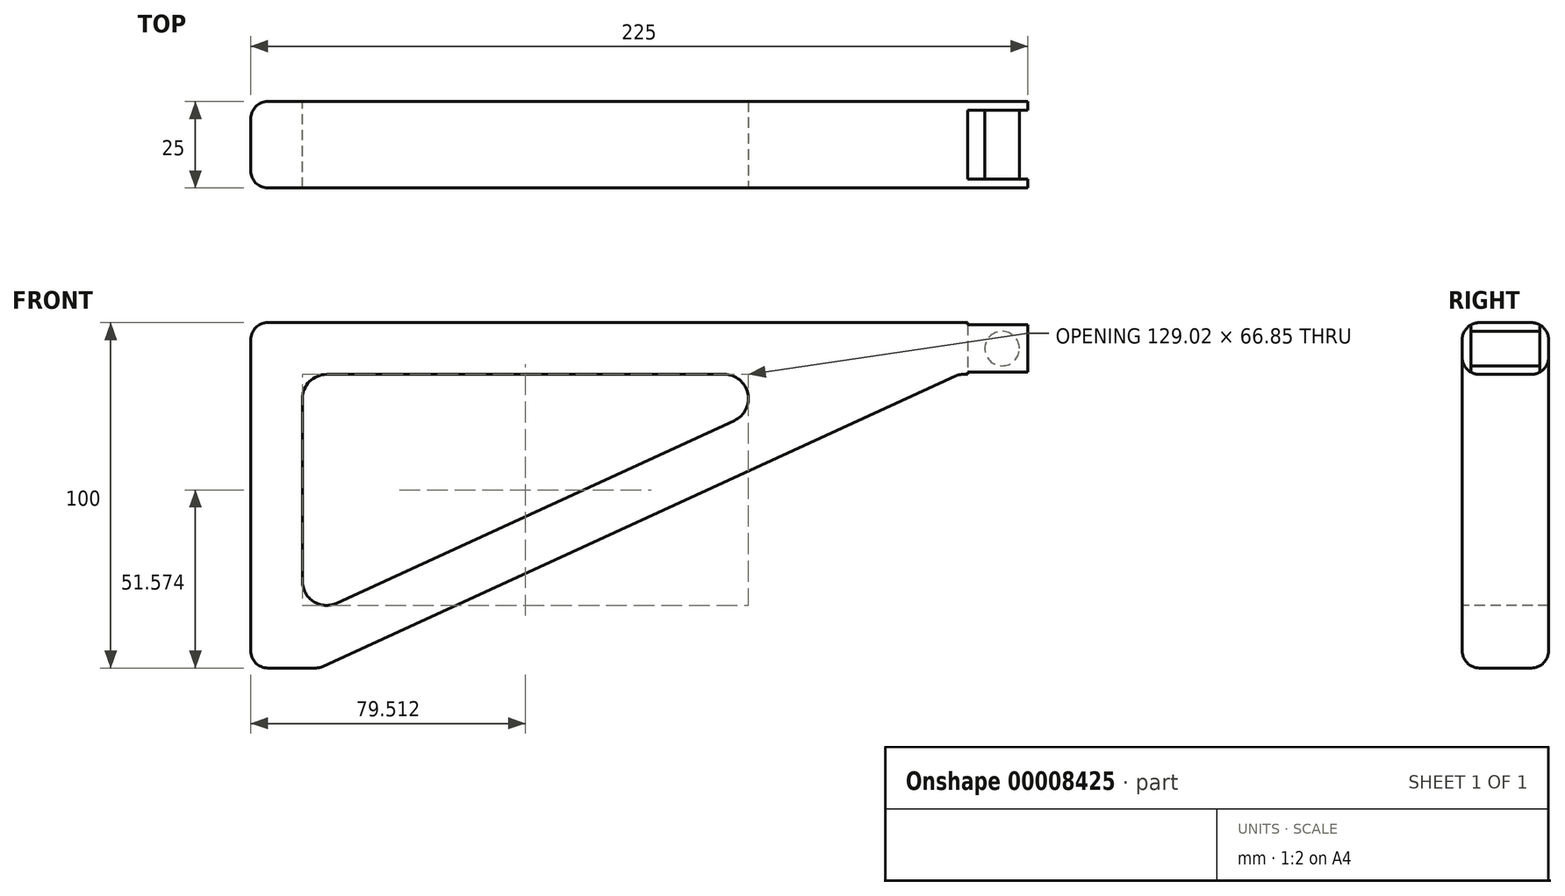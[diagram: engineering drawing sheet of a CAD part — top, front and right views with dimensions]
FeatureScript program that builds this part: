
annotation { "Feature Type Name" : "Feature", "Feature Type Description" : "" }
export const myFeature = defineFeature(function(context is Context, id is Id, definition is map)
    precondition{}
    {
        {
            var Q0;
            Q0=qCreatedBy(makeId("Front.planeOp"),FACE);
            var sketch = newSketch(context, id + "F0", { "sketchPlane" : qUnion([Q0])});
            skLineSegment(sketch, "E0", {"start": v(51.64, 0) * mm, "end": v(-173.36, 0) * mm});
            skLineSegment(sketch, "E1", {"start": v(-173.36, 0) * mm, "end": v(-173.36, -100) * mm});
            skLineSegment(sketch, "E2", {"start": v(-173.36, -100) * mm, "end": v(-153.36, -100) * mm});
            skLineSegment(sketch, "E3", {"start": v(-153.36, -100) * mm, "end": v(31.64, -15) * mm});
            skLineSegment(sketch, "E4", {"start": v(31.64, -15) * mm, "end": v(51.64, -15) * mm});
            skLineSegment(sketch, "E5", {"start": v(51.64, -15) * mm, "end": v(51.64, 0) * mm});
            skSolve(sketch);
        }
        {
            var Q0;
            Q0 = qSketchRegion(id + "F0", true);
            extrude(context, id + "F1", {"entities" : qUnion([Q0]), "depth" : 25 * mm});
        }
        {
            var Q0;
            Q0=makeQuery(id+"F1.opExtrude","SWEPT_FACE",FACE,{"disambiguationData":[OSD([sQuery(id+"F0.wireOp",EDGE,"E4")])]});
            var sketch = newSketch(context, id + "F2", { "sketchPlane" : qUnion([Q0])});
            skLineSegment(sketch, "E6.bottom", {"start": v(51.64, 2.5) * mm, "end": v(34.14, 2.5) * mm});
            skLineSegment(sketch, "E6.top", {"start": v(51.64, 22.5) * mm, "end": v(34.14, 22.5) * mm});
            skLineSegment(sketch, "E6.left", {"start": v(51.64, 2.5) * mm, "end": v(51.64, 22.5) * mm});
            skLineSegment(sketch, "E6.right", {"start": v(34.14, 2.5) * mm, "end": v(34.14, 22.5) * mm});
            skSolve(sketch);
        }
        {
            var Q0;
            Q0 = qSketchRegion(id + "F2", true);
            extrude(context, id + "F3", {"entities" : qUnion([Q0]), "operationType" : NewBodyOperationType.REMOVE, "oppositeDirection" : true, "depth" : 25 * mm});
        }
        {
            var Q0;
            Q0=makeQuery(id+"F1.opExtrude","CAP_FACE",FACE,{"disambiguationData":[OSD([sQuery(id+"F0.wireOp",EDGE,"E0"),sQuery(id+"F0.wireOp",EDGE,"E1"),sQuery(id+"F0.wireOp",EDGE,"E2"),sQuery(id+"F0.wireOp",EDGE,"E3"),sQuery(id+"F0.wireOp",EDGE,"E4"),sQuery(id+"F0.wireOp",EDGE,"E5")])],"isStart":false});
            var sketch = newSketch(context, id + "F4", { "sketchPlane" : qUnion([Q0])});
            skCircle(sketch, "E7", {"center": v(44.14, -7.5) * mm, "radius": 5 * mm});
            skSolve(sketch);
        }
        {
            var Q0;
            Q0 = qSketchRegion(id + "F4", true);
            extrude(context, id + "F5", {"entities" : qUnion([Q0]), "operationType" : NewBodyOperationType.ADD, "oppositeDirection" : true, "depth" : 25 * mm});
        }
        {
            var Q0;
            Q0=makeQuery(id+"F1.opExtrude","CAP_EDGE",EDGE,{"disambiguationData":[OSD([sQuery(id+"F0.wireOp",EDGE,"E1")])],"isStart":false});
            var Q1;
            Q1=makeQuery(id+"F1.opExtrude","CAP_EDGE",EDGE,{"disambiguationData":[OSD([sQuery(id+"F0.wireOp",EDGE,"E1")])],"isStart":true});
            var Q2;
            Q2=makeQuery(id+"F1.opExtrude","CAP_EDGE",EDGE,{"disambiguationData":[OSD([sQuery(id+"F0.wireOp",EDGE,"E0")])],"isStart":false});
            var Q3;
            Q3=makeQuery(id+"F1.opExtrude","CAP_EDGE",EDGE,{"disambiguationData":[OSD([sQuery(id+"F0.wireOp",EDGE,"E0")])],"isStart":true});
            var Q4;
            Q4=makeQuery(id+"F1.opExtrude","CAP_EDGE",EDGE,{"disambiguationData":[OSD([sQuery(id+"F0.wireOp",EDGE,"E4")])],"isStart":false});
            var Q5;
            Q5=makeQuery(id+"F1.opExtrude","CAP_EDGE",EDGE,{"disambiguationData":[OSD([sQuery(id+"F0.wireOp",EDGE,"E4")])],"isStart":true});
            var Q6;
            Q6=makeQuery(id+"F1.opExtrude","CAP_EDGE",EDGE,{"disambiguationData":[OSD([sQuery(id+"F0.wireOp",EDGE,"E3")])],"isStart":false});
            var Q7;
            Q7=makeQuery(id+"F1.opExtrude","CAP_EDGE",EDGE,{"disambiguationData":[OSD([sQuery(id+"F0.wireOp",EDGE,"E3")])],"isStart":true});
            var Q8;
            Q8=makeQuery(id+"F1.opExtrude","CAP_EDGE",EDGE,{"disambiguationData":[OSD([sQuery(id+"F0.wireOp",EDGE,"E2")])],"isStart":false});
            var Q9;
            Q9=makeQuery(id+"F1.opExtrude","CAP_EDGE",EDGE,{"disambiguationData":[OSD([sQuery(id+"F0.wireOp",EDGE,"E2")])],"isStart":true});
            var Q10;
            Q10=makeQuery(id+"F1.opExtrude","SWEPT_EDGE",EDGE,{"disambiguationData":[OSD([sQuery(id+"F0.wireOp",EDGE,"E2"),sQuery(id+"F0.wireOp",EDGE,"E3")])]});
            var Q11;
            Q11=makeQuery(id+"F1.opExtrude","SWEPT_EDGE",EDGE,{"disambiguationData":[OSD([sQuery(id+"F0.wireOp",EDGE,"E1"),sQuery(id+"F0.wireOp",EDGE,"E2")])]});
            var Q12;
            Q12=makeQuery(id+"F1.opExtrude","SWEPT_EDGE",EDGE,{"disambiguationData":[OSD([sQuery(id+"F0.wireOp",EDGE,"E0"),sQuery(id+"F0.wireOp",EDGE,"E1")])]});
            var Q13;
            Q13=makeQuery(id+"F1.opExtrude","SWEPT_EDGE",EDGE,{"disambiguationData":[OSD([sQuery(id+"F0.wireOp",EDGE,"E3"),sQuery(id+"F0.wireOp",EDGE,"E4")])]});
            fillet(context, id + "F6", {"entities" : qUnion([Q0, Q1, Q2, Q3, Q4, Q5, Q6, Q7, Q8, Q9, Q10, Q11, Q12, Q13]), "radius" : 5 * mm, "tangentPropagation" : true, "allowEdgeOverflow" : false});
        }
        {
            var Q0;
            Q0=makeQuery(id+"F1.opExtrude","CAP_FACE",FACE,{"disambiguationData":[OSD([sQuery(id+"F0.wireOp",EDGE,"E0"),sQuery(id+"F0.wireOp",EDGE,"E1"),sQuery(id+"F0.wireOp",EDGE,"E2"),sQuery(id+"F0.wireOp",EDGE,"E3"),sQuery(id+"F0.wireOp",EDGE,"E4"),sQuery(id+"F0.wireOp",EDGE,"E5")])],"isStart":true});
            var sketch = newSketch(context, id + "F7", { "sketchPlane" : qUnion([Q0])});
            skLineSegment(sketch, "E8", {"start": v(4.28, -15) * mm, "end": v(158.36, -15) * mm});
            skLineSegment(sketch, "E9", {"start": v(158.36, -15) * mm, "end": v(158.36, -85.79) * mm});
            skLineSegment(sketch, "E10", {"start": v(158.36, -85.79) * mm, "end": v(4.28, -15) * mm});
            skSolve(sketch);
        }
        {
            var Q0;
            Q0 = qSketchRegion(id + "F7", true);
            extrude(context, id + "F8", {"entities" : qUnion([Q0]), "operationType" : NewBodyOperationType.REMOVE, "oppositeDirection" : true, "depth" : 25 * mm});
        }
        {
            var Q0;
            Q0=makeQuery(id+"F8.boolean.opBoolean","COPY",EDGE,{"derivedFrom":makeQuery(id+"F8.opExtrude","SWEPT_EDGE",EDGE,{"disambiguationData":[OSD([sQuery(id+"F7.wireOp",EDGE,"E9"),sQuery(id+"F7.wireOp",EDGE,"E10")])]})});
            var Q1;
            Q1=makeQuery(id+"F8.boolean.opBoolean","COPY",EDGE,{"derivedFrom":makeQuery(id+"F8.opExtrude","SWEPT_EDGE",EDGE,{"disambiguationData":[OSD([sQuery(id+"F7.wireOp",EDGE,"E8"),sQuery(id+"F7.wireOp",EDGE,"E9")])]})});
            var Q2;
            Q2=makeQuery(id+"F8.boolean.opBoolean","COPY",EDGE,{"derivedFrom":makeQuery(id+"F8.opExtrude","SWEPT_EDGE",EDGE,{"disambiguationData":[OSD([sQuery(id+"F7.wireOp",EDGE,"E8"),sQuery(id+"F7.wireOp",EDGE,"E10")])]})});
            var Q3;
            Q3=makeQuery(id+"F8.boolean.opBoolean","COPY",EDGE,{"derivedFrom":makeQuery(id+"F8.opExtrude","CAP_EDGE",EDGE,{"disambiguationData":[OSD([sQuery(id+"F7.wireOp",EDGE,"E8")])],"isStart":true})});
            var Q4;
            Q4=makeQuery(id+"F8.boolean.opBoolean","COPY",EDGE,{"derivedFrom":makeQuery(id+"F8.opExtrude","CAP_EDGE",EDGE,{"disambiguationData":[OSD([sQuery(id+"F7.wireOp",EDGE,"E8")])],"isStart":false})});
            fillet(context, id + "F9", {"entities" : qUnion([Q0, Q1, Q2, Q3, Q4]), "radius" : 7 * mm, "tangentPropagation" : true, "allowEdgeOverflow" : false});
        }
    });
